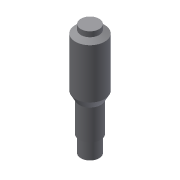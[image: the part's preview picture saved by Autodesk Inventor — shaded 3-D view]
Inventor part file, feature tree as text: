
AUTODESK INVENTOR PART (.ipt)
format: ipt  version: 2019.4 (Build 234330000, 330)  size: 98,304 bytes
history: native  units: mm
features: revolve x1, sketch x1
ambient origin geometry x8: Origin, YZ Plane, XZ Plane, XY Plane, X Axis, Y Axis, Z Axis, Center Point
bodies: Solid1 (feature_tree)
feature tree (2):
  revolve  "Revolution1"  [1 undecoded]
  sketch  "Sketch1"  dims[d0=1.725mm d1=0.86mm d2=1.28mm d3=90.0deg d4=5.5mm d5=0.5mm d6=9.92mm d7=4.815mm d8=37.64mm d9=90.0deg]
note: 1 required parameter value undecoded (feature->parameter linkage not recoverable at this tier; creation-order binding heuristic only, values carry confidence <= 0.55)
